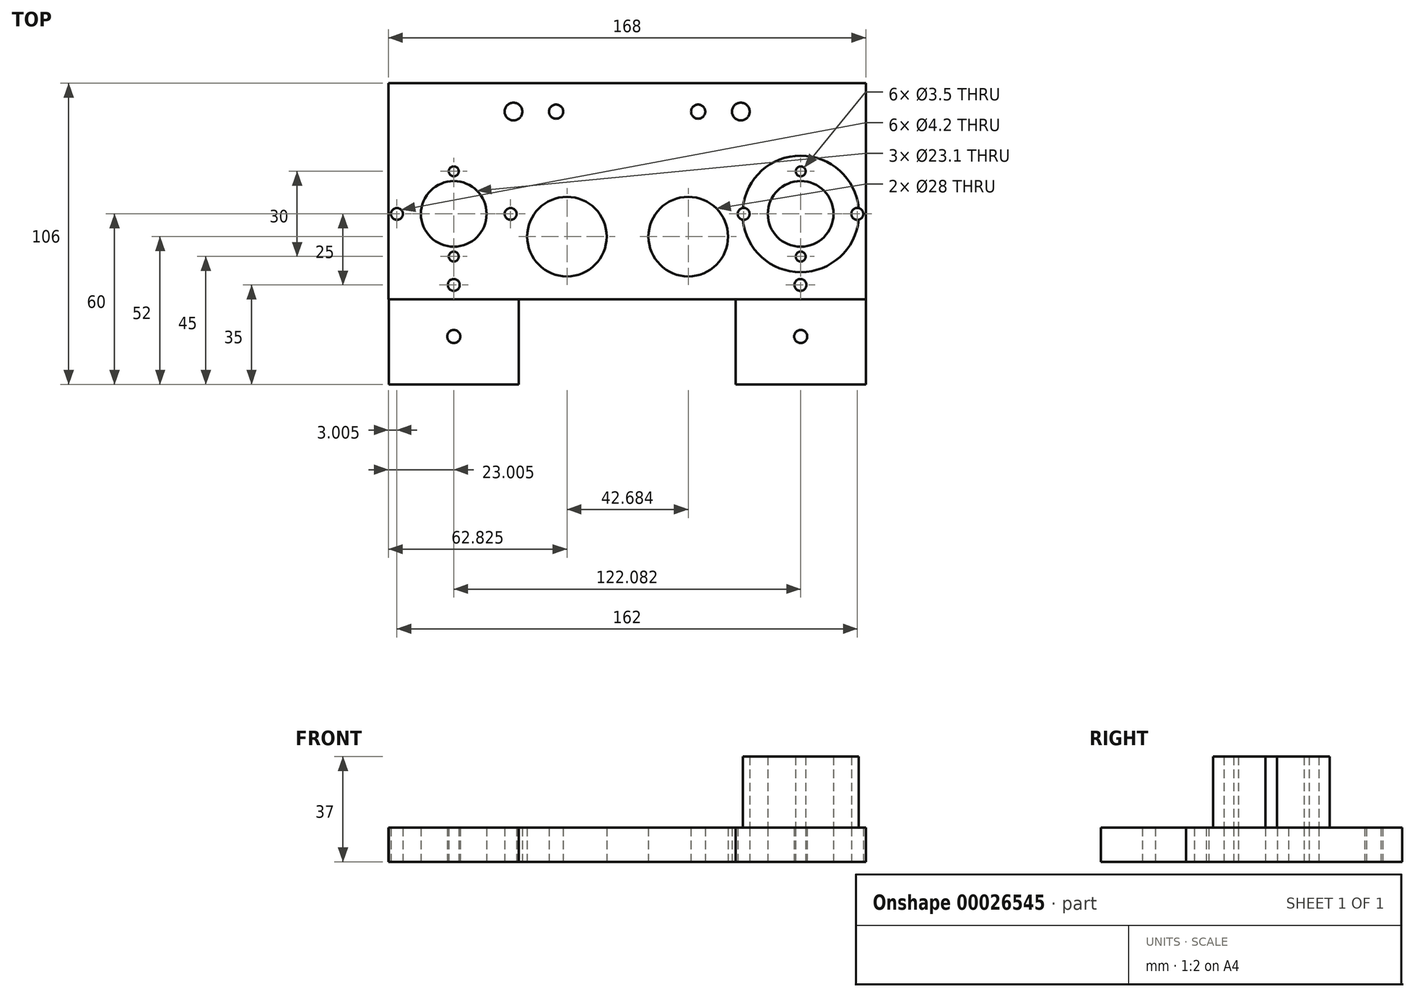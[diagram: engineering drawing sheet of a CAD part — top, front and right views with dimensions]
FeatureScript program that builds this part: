
annotation { "Feature Type Name" : "Feature", "Feature Type Description" : "" }
export const myFeature = defineFeature(function(context is Context, id is Id, definition is map)
    precondition{}
    {
        {
            var Q0;
            Q0=qCreatedBy(makeId("Top.planeOp"),FACE);
            var sketch = newSketch(context, id + "F0", { "sketchPlane" : qUnion([Q0])});
            skCircle(sketch, "E0", {"center": v(-57, -16.5) * mm, "radius": 11.55 * mm});
            skCircle(sketch, "E1", {"center": v(65.09, -16.5) * mm, "radius": 11.55 * mm});
            skCircle(sketch, "E2", {"center": v(25.5, -24.5) * mm, "radius": 14 * mm});
            skCircle(sketch, "E3", {"center": v(-17.18, -24.5) * mm, "radius": 14 * mm});
            skLineSegment(sketch, "E4.top", {"start": v(-80, -46.5) * mm, "end": v(88, -46.5) * mm});
            skLineSegment(sketch, "E4.left", {"start": v(-80, 29.5) * mm, "end": v(-80, -46.5) * mm});
            skLineSegment(sketch, "E4.right", {"start": v(88, 29.5) * mm, "end": v(88, -46.5) * mm});
            skLineSegment(sketch, "E5.filletArc", {"start": v(88, -46.5) * mm, "end": v(88, -46.5) * mm});
            skLineSegment(sketch, "E6.filletArc", {"start": v(-80, -46.5) * mm, "end": v(-80, -46.5) * mm});
            skLineSegment(sketch, "E7.0", {"start": v(-80, 29.5) * mm, "end": v(88, 29.5) * mm});
            skLineSegment(sketch, "E8", {"start": v(65.09, -16.5) * mm, "end": v(-213.1, -16.5) * mm, "construction": true});
            skCircle(sketch, "E9", {"center": v(44, 19.5) * mm, "radius": 3.12 * mm});
            skCircle(sketch, "E10", {"center": v(29, 19.5) * mm, "radius": 2.5 * mm});
            skCircle(sketch, "E11", {"center": v(-21, 19.5) * mm, "radius": 2.5 * mm});
            skCircle(sketch, "E12", {"center": v(-36, 19.5) * mm, "radius": 3.12 * mm});
            skLineSegment(sketch, "E13", {"start": v(4, 29.5) * mm, "end": v(4, -84.57) * mm, "construction": true});
            skCircle(sketch, "E14", {"center": v(-57, -31.5) * mm, "radius": 1.75 * mm});
            skCircle(sketch, "E15", {"center": v(-57, -1.5) * mm, "radius": 1.75 * mm});
            skCircle(sketch, "E16", {"center": v(65.09, -31.5) * mm, "radius": 1.75 * mm});
            skCircle(sketch, "E17", {"center": v(65.09, -1.5) * mm, "radius": 1.75 * mm});
            skCircle(sketch, "E18", {"center": v(-57, -16.5) * mm, "radius": 15 * mm, "construction": true});
            skCircle(sketch, "E19", {"center": v(-37, -16.5) * mm, "radius": 2.1 * mm});
            skCircle(sketch, "E20", {"center": v(-77, -16.5) * mm, "radius": 2.1 * mm});
            skCircle(sketch, "E21", {"center": v(-57, -41.5) * mm, "radius": 2.1 * mm});
            skCircle(sketch, "E22.MirrorC", {"center": v(85, -16.5) * mm, "radius": 2.1 * mm});
            skCircle(sketch, "E23.MirrorC", {"center": v(65, -41.5) * mm, "radius": 2.1 * mm});
            skCircle(sketch, "E24.MirrorC", {"center": v(45, -16.5) * mm, "radius": 2.1 * mm});
            skSolve(sketch);
        }
        {
            var Q0;
            Q0=qSketchRegion(id+"F0",true);
            extrude(context, id + "F1", {"entities" : qUnion([Q0]), "depth" : 12 * mm});
        }
        {
            var Q0;
            Q0=makeQuery(id+"F1.opExtrude","CAP_FACE",FACE,{"disambiguationData":[OSD([sQuery(id+"F0.wireOp",EDGE,"E0"),sQuery(id+"F0.wireOp",EDGE,"E1"),sQuery(id+"F0.wireOp",EDGE,"E2"),sQuery(id+"F0.wireOp",EDGE,"E3"),sQuery(id+"F0.wireOp",EDGE,"E4.top"),sQuery(id+"F0.wireOp",EDGE,"E4.left"),sQuery(id+"F0.wireOp",EDGE,"E4.right"),sQuery(id+"F0.wireOp",EDGE,"E5.filletArc"),sQuery(id+"F0.wireOp",EDGE,"E6.filletArc"),sQuery(id+"F0.wireOp",EDGE,"E7.0"),sQuery(id+"F0.wireOp",EDGE,"E9"),sQuery(id+"F0.wireOp",EDGE,"E10"),sQuery(id+"F0.wireOp",EDGE,"E11"),sQuery(id+"F0.wireOp",EDGE,"E12")])],"isStart":false});
            var sketch = newSketch(context, id + "F2", { "sketchPlane" : qUnion([Q0])});
            skCircle(sketch, "E25", {"center": v(65.09, -16.5) * mm, "radius": 20.5 * mm});
            skCircle(sketch, "E26.0", {"center": v(65.09, -16.5) * mm, "radius": 11.55 * mm});
            skSolve(sketch);
        }
        {
            var Q0;
            Q0=makeQuery(id+"F2.imprint","IMPRINT",FACE,{"disambiguationData":[TD([[makeQuery(id+"F2.imprint","IMPRINT",EDGE,{"derivedFrom":sQuery(id+"F2.wireOp",EDGE,"E25")}),1.0]])]});
            extrude(context, id + "F3", {"entities" : qUnion([Q0]), "depth" : 25 * mm});
        }
        {
            var Q0;
            Q0=makeQuery(id+"F0.imprint","IMPRINT",FACE,{"disambiguationData":[TD([[makeQuery(id+"F0.imprint","IMPRINT",EDGE,{"derivedFrom":sQuery(id+"F0.wireOp",EDGE,"E0")}),-1.0]])]});
            var sketch = newSketch(context, id + "F4", { "sketchPlane" : qUnion([Q0])});
            skPoint(sketch, "E27.0", {"position": v(-57, -16.5) * mm});
            skPoint(sketch, "E28.0", {"position": v(65.09, -16.5) * mm});
            skLineSegment(sketch, "E29", {"start": v(-57, -16.5) * mm, "end": v(120.3, -16.5) * mm, "construction": true});
            skLineSegment(sketch, "E30", {"start": v(-57, 53.93) * mm, "end": v(-57, -87) * mm, "construction": true});
            skLineSegment(sketch, "E31", {"start": v(65.09, 53.48) * mm, "end": v(65.09, -91.61) * mm, "construction": true});
            skLineSegment(sketch, "E32.0", {"start": v(-79.9, -46.5) * mm, "end": v(-79.9, -76.5) * mm});
            skLineSegment(sketch, "E33.0", {"start": v(-34.1, -46.5) * mm, "end": v(-34.1, -76.5) * mm});
            skLineSegment(sketch, "E34.0", {"start": v(42.19, -46.5) * mm, "end": v(42.19, -76.5) * mm});
            skLineSegment(sketch, "E35.0", {"start": v(87.99, -46.5) * mm, "end": v(87.99, -76.5) * mm});
            skCircle(sketch, "E36", {"center": v(-57, -59.65) * mm, "radius": 2.3 * mm});
            skCircle(sketch, "E37", {"center": v(65.09, -59.65) * mm, "radius": 2.3 * mm});
            skLineSegment(sketch, "E38.0", {"start": v(-79.9, -46.5) * mm, "end": v(-34.1, -46.5) * mm});
            skLineSegment(sketch, "E39.0", {"start": v(42.19, -46.5) * mm, "end": v(87.99, -46.5) * mm});
            skPoint(sketch, "E40.orphan", {"position": v(88, 29.5) * mm});
            skPoint(sketch, "E41.orphan", {"position": v(-80, 29.5) * mm});
            skLineSegment(sketch, "E42.0", {"start": v(42.19, -76.5) * mm, "end": v(87.99, -76.5) * mm});
            skLineSegment(sketch, "E43.0", {"start": v(-79.9, -76.5) * mm, "end": v(-34.1, -76.5) * mm});
            skSolve(sketch);
        }
        {
            var Q0;
            Q0=makeQuery(id+"F4.imprint","IMPRINT",FACE,{"disambiguationData":[TD([[makeQuery(id+"F4.imprint","IMPRINT",EDGE,{"derivedFrom":sQuery(id+"F4.wireOp",EDGE,"E34.0")}),1.0]])]});
            var Q1;
            Q1=makeQuery(id+"F4.imprint","IMPRINT",FACE,{"disambiguationData":[TD([[makeQuery(id+"F4.imprint","IMPRINT",EDGE,{"derivedFrom":sQuery(id+"F4.wireOp",EDGE,"E32.0")}),1.0]])]});
            extrude(context, id + "F5", {"entities" : qUnion([Q0, Q1]), "depth" : 12 * mm, "offsetDistance" : 25 * mm});
        }
    });
